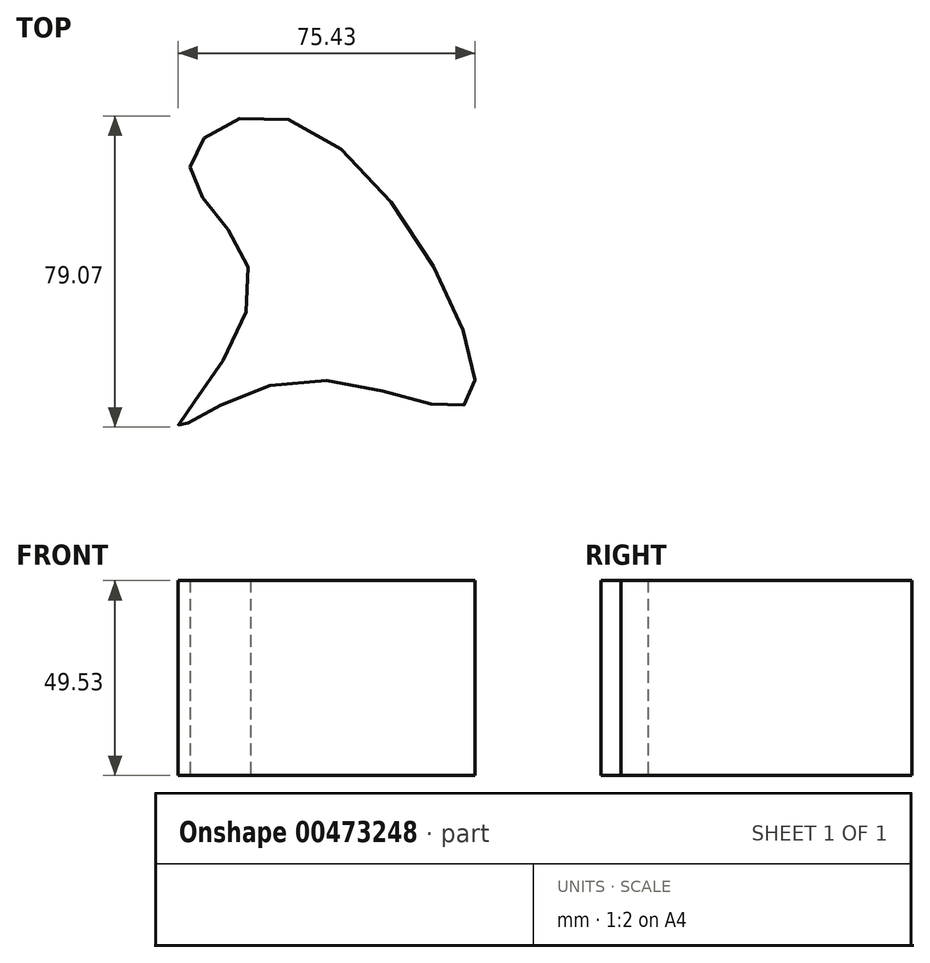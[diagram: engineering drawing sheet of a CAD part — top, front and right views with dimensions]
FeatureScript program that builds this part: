
annotation { "Feature Type Name" : "Feature", "Feature Type Description" : "" }
export const myFeature = defineFeature(function(context is Context, id is Id, definition is map)
    precondition{}
    {
        {
            var Q0;
            Q0=qCreatedBy(makeId("Top.planeOp"),FACE);
            var sketch = newSketch(context, id + "F0", { "sketchPlane" : qUnion([Q0])});
            skFitSpline(sketch, "E0", {"points": [v(-28.08, 29.9) * mm, v(0, 40.95) * mm, v(43.52, -28.69) * mm, v(0, -24.3) * mm, v(-31.11, -35.96) * mm, v(-12.64, 0) * mm, v(-28.08, 29.9) * mm]});
            skSolve(sketch);
        }
        {
            var Q0;
            Q0=makeQuery(id+"F0.imprint","IMPRINT",FACE,{"disambiguationData":[TD([[makeQuery(id+"F0.imprint","IMPRINT",EDGE,{"derivedFrom":sQuery(id+"F0.wireOp",EDGE,"E0")}),-1.0]])]});
            extrude(context, id + "F1", {"entities" : qUnion([Q0]), "depth" : 49.53 * mm});
        }
    });
